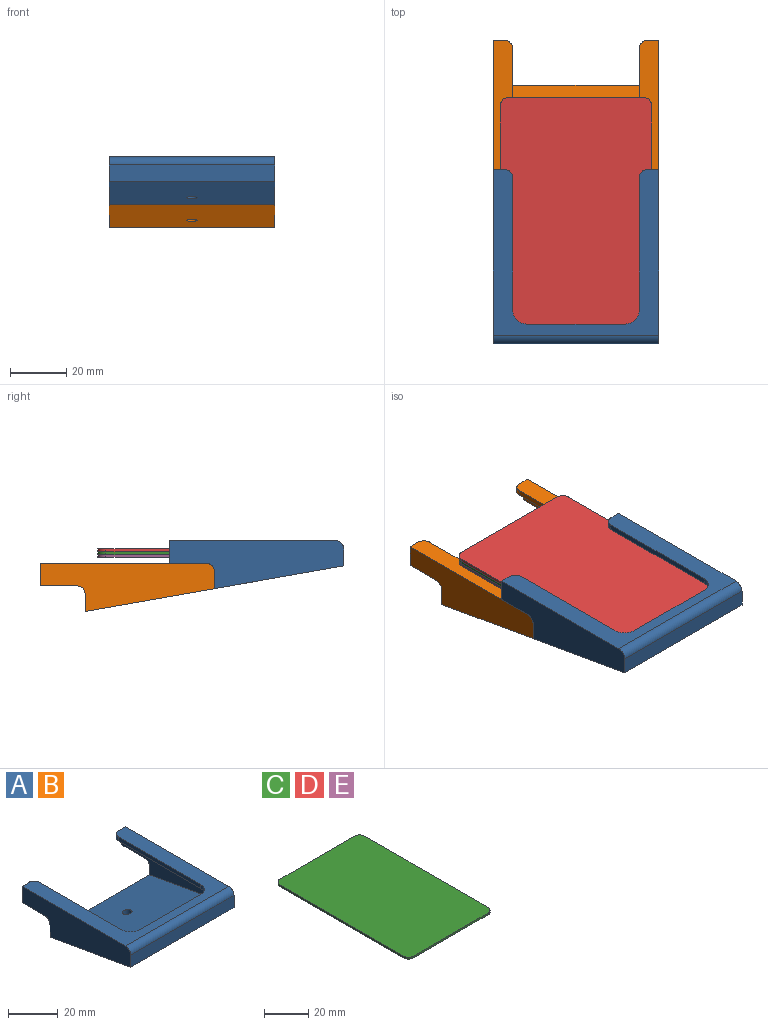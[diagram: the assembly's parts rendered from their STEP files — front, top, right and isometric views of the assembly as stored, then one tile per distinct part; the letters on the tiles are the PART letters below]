
ASSEMBLY  parts=5 mates=4
PART A: 26 faces, bbox 59x62x17.1 mm
  f0: plane 59x6.11mm, normal (0,1,0), area 153.8mm2, adj f1,f2,f5,f6,f7,f9,f21,f22
  f1: plane 60x12.76mm, normal (-1,0,0), area 488.6mm2, adj f0,f3,f5,f13,f18,f20,f21
  f2: plane 60x12.76mm, normal (1,0,0), area 488.6mm2, adj f0,f3,f5,f12,f18,f19,f22
  f3: plane 55x5mm, normal (0,1,0), area 275mm2, adj f1,f2,f5,f18
  f4: cylinder r=2mm len=4mm, axis (0,0,-1), area 29.6mm2, adj f5,f6
  f5: plane 55x44mm, normal (0,0.17,0.98), area 2444.6mm2, adj f0,f1,f2,f3,f4
  f6: plane 59x46mm, normal (0,-0.17,-0.98), area 2743.1mm2, adj f0,f4,f7,f8,f9
  f7: plane 62x17.11mm, normal (-1,0,0), area 728.6mm2, adj f0,f6,f8,f10,f12,f19,f22,f25
  f8: plane 59x6mm, normal (0,-1,0), area 354mm2, adj f6,f7,f9,f25
  f9: plane 62x17.11mm, normal (1,0,0), area 728.6mm2, adj f0,f6,f8,f10,f13,f20,f21,f25
  f10: plane 59x59mm, normal (0,0,1), area 1012.9mm2, adj f7,f9,f11,f12,f13,f14,f15,f16
  f11: plane 47x2mm, normal (1,0,0), area 94mm2, adj f10,f17,f18,f23
  f12: plane 8x4mm, normal (0,1,0), area 20mm2, adj f2,f7,f10,f18,f19,f23
  f13: plane 8x4mm, normal (0,1,0), area 20mm2, adj f1,f9,f10,f18,f20,f24
  f14: plane 47x2mm, normal (-1,0,0), area 94mm2, adj f10,f15,f18,f24
  f15: cylinder r=5mm len=5mm, axis (0,0,-1), area 15.7mm2, adj f10,f14,f16,f18
  f16: plane 35x2mm, normal (0,1,0), area 70mm2, adj f10,f15,f17,f18
  f17: cylinder r=5mm len=5mm, axis (0,0,-1), area 15.7mm2, adj f10,f11,f16,f18
  f18: plane 60x55mm, normal (0,0,-1), area 831.9mm2, adj f1,f2,f3,f11,f12,f13,f14,f15
  f19: plane 13x2mm, normal (0,0,-1), area 26mm2, adj f2,f7,f12,f22
  f20: plane 13x2mm, normal (0,0,-1), area 26mm2, adj f1,f9,f13,f21
  f21: cylinder r=3mm len=3mm, axis (1,0,0), area 9.4mm2, adj f0,f1,f9,f20
  f22: cylinder r=3mm len=3mm, axis (-1,0,0), area 9.4mm2, adj f0,f2,f7,f19
  f23: cylinder r=3mm len=3mm, axis (0,0,-1), area 9.4mm2, adj f10,f11,f12,f18
  f24: cylinder r=3mm len=3mm, axis (0,0,1), area 9.4mm2, adj f10,f13,f14,f18
  f25: cylinder r=3mm len=59mm, axis (-1,0,0), area 278mm2, adj f7,f8,f9,f10
PART B: same geometry as A
PART C: 10 faces, bbox 54x85.6x1 mm
  f0: plane 47.98x1mm, normal (0,-1,0), area 48mm2, adj f1,f7,f8,f9
  f1: cylinder r=3mm len=3mm, axis (0,0,-1), area 4.7mm2, adj f0,f2,f8,f9
  f2: plane 79.6x1mm, normal (1,0,0), area 79.6mm2, adj f1,f3,f8,f9
  f3: cylinder r=3mm len=3mm, axis (0,0,-1), area 4.7mm2, adj f2,f4,f8,f9
  f4: plane 47.98x1mm, normal (0,1,0), area 48mm2, adj f3,f5,f8,f9
  f5: cylinder r=3mm len=3mm, axis (0,0,-1), area 4.7mm2, adj f4,f6,f8,f9
  f6: plane 79.6x1mm, normal (-1,0,0), area 79.6mm2, adj f5,f7,f8,f9
  f7: cylinder r=3mm len=3mm, axis (0,0,-1), area 4.7mm2, adj f0,f6,f8,f9
  f8: plane 85.6x53.98mm, normal (0,0,1), area 4613mm2, adj f0,f1,f2,f3,f4,f5,f6,f7
  f9: plane 85.6x53.98mm, normal (0,0,-1), area 4613mm2, adj f0,f1,f2,f3,f4,f5,f6,f7
PART D: same geometry as C
PART E: same geometry as C
PLACE A t=(2.99,-46.72,7.6)mm
PLACE B t=(2.99,-0.72,-0.51)mm
PLACE C t=(2.99,-3.92,11.6)mm
PLACE D t=(2.99,-3.92,12.6)mm
PLACE E t=(2.99,-3.92,10.6)mm
MATE fastened E.f0 <-> C.f0  axis (0,-1,0) through (2.99,-46.72,11.1)mm
MATE fastened A.f3 <-> C.f0  axis (0,1,0) through (2.99,-46.72,12.1)mm
MATE fastened D.f0 <-> C.f0  axis (0,-1,0) through (2.99,-46.72,13.1)mm
MATE fastened B.f7 <-> A.f7  axis (1,0,0) through (-26.51,-2.72,-0.51)mm
